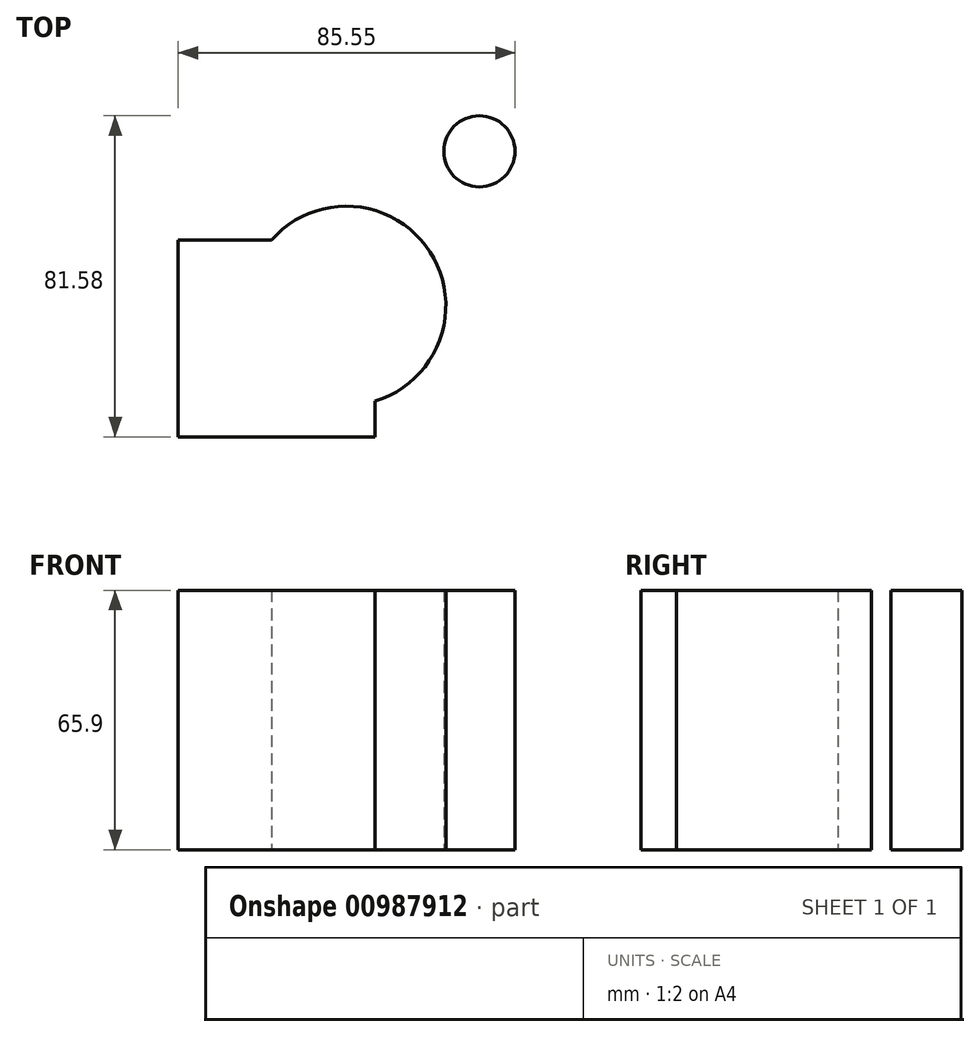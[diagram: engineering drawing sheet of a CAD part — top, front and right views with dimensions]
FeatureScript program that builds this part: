
annotation { "Feature Type Name" : "Feature", "Feature Type Description" : "" }
export const myFeature = defineFeature(function(context is Context, id is Id, definition is map)
    precondition{}
    {
        {
            var Q0;
            Q0=qCreatedBy(makeId("Top.planeOp"),FACE);
            var sketch = newSketch(context, id + "F0", { "sketchPlane" : qUnion([Q0])});
            skLineSegment(sketch, "E0.bottom", {"start": v(-25, 25) * mm, "end": v(25, 25) * mm});
            skLineSegment(sketch, "E0.top", {"start": v(-25, -25) * mm, "end": v(25, -25) * mm});
            skLineSegment(sketch, "E0.left", {"start": v(-25, 25) * mm, "end": v(-25, -25) * mm});
            skLineSegment(sketch, "E0.right", {"start": v(25, 25) * mm, "end": v(25, -25) * mm});
            skPoint(sketch, "E0.middle", {"position": v(0, 0) * mm});
            skCircle(sketch, "E1", {"center": v(17.7, 8.3) * mm, "radius": 25.3 * mm});
            skCircle(sketch, "E2", {"center": v(51.52, 47.55) * mm, "radius": 9.03 * mm});
            skSolve(sketch);
        }
        {
            var Q0;
            Q0=makeQuery(id+"F0.imprint","IMPRINT",FACE,{"disambiguationData":[TD([[makeQuery(id+"F0.imprint","IMPRINT",EDGE,{"derivedFrom":sQuery(id+"F0.wireOp",EDGE,"E0.bottom")}),-1.0]])]});
            extrude(context, id + "F1", {"entities" : qUnion([Q0]), "depth" : 50 * mm, "offsetDistance" : 25 * mm});
        }
        {
            var Q0;
            Q0 = qSketchRegion(id + "F0", true);
            extrude(context, id + "F2", {"entities" : qUnion([Q0]), "operationType" : NewBodyOperationType.ADD, "depth" : 65.9 * mm, "offsetDistance" : 25 * mm});
        }
    });
